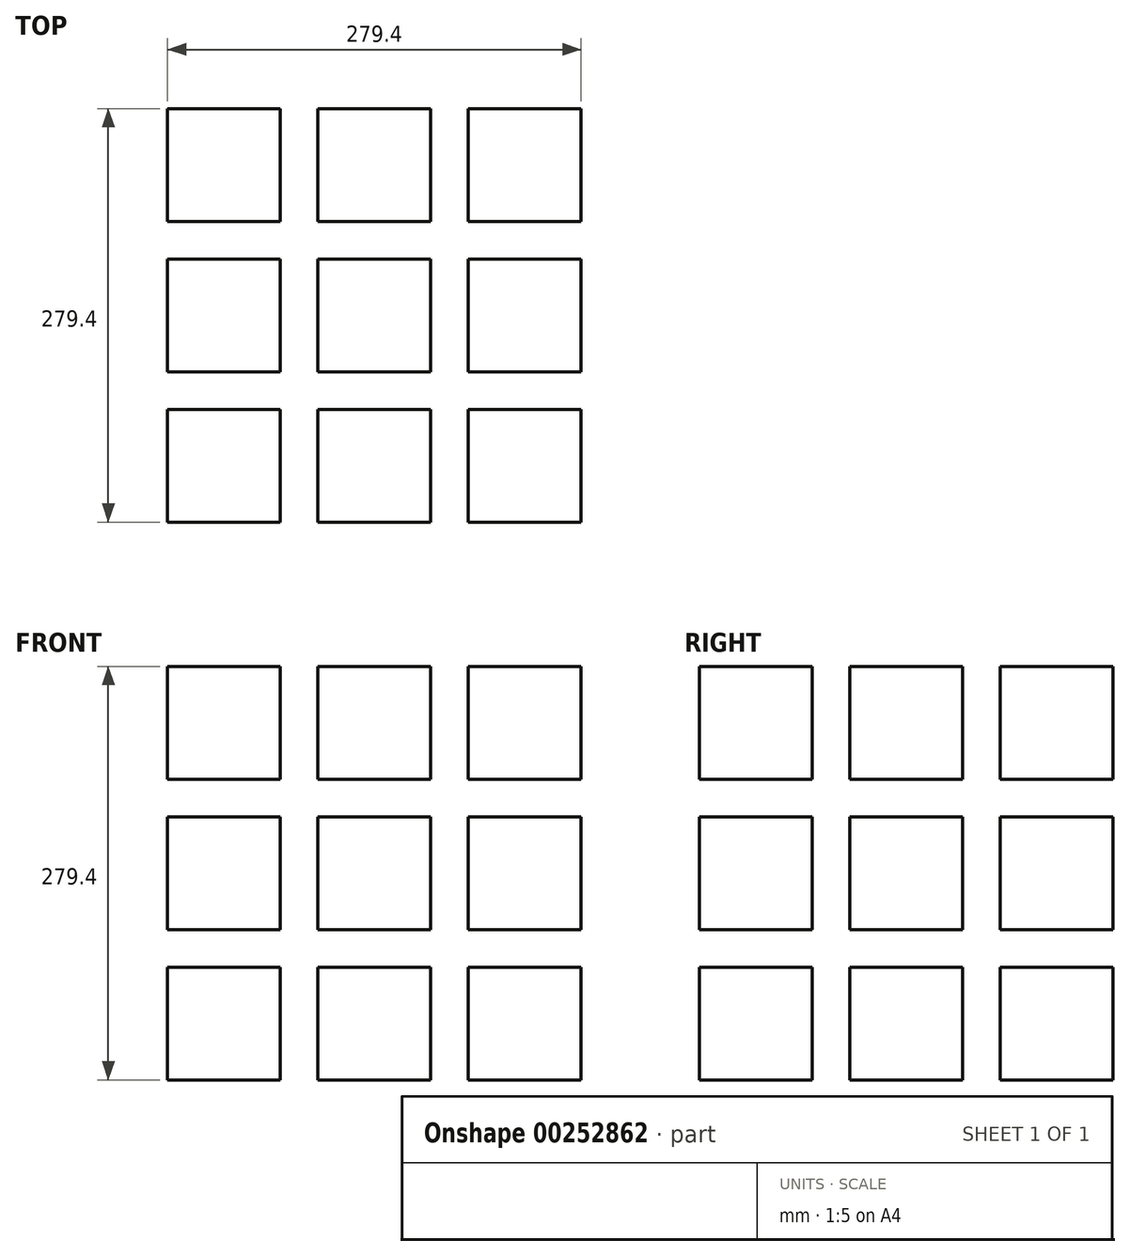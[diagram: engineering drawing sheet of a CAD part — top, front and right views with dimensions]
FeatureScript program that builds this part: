
annotation { "Feature Type Name" : "Feature", "Feature Type Description" : "" }
export const myFeature = defineFeature(function(context is Context, id is Id, definition is map)
    precondition{}
    {
        {
            var Q0;
            Q0=qCreatedBy(makeId("Top.planeOp"),FACE);
            var sketch = newSketch(context, id + "F0", { "sketchPlane" : qUnion([Q0])});
            skLineSegment(sketch, "E0.bottom", {"start": v(139.7, -139.7) * mm, "end": v(-139.7, -139.7) * mm});
            skLineSegment(sketch, "E0.top", {"start": v(139.7, 139.7) * mm, "end": v(-139.7, 139.7) * mm});
            skLineSegment(sketch, "E0.left", {"start": v(139.7, -139.7) * mm, "end": v(139.7, 139.7) * mm});
            skLineSegment(sketch, "E0.right", {"start": v(-139.7, -139.7) * mm, "end": v(-139.7, 139.7) * mm});
            skPoint(sketch, "E0.middle", {"position": v(0, 0) * mm});
            skSolve(sketch);
        }
        {
            var Q0;
            Q0=makeQuery(id+"F0.imprint","IMPRINT",FACE,{"disambiguationData":[TD([[makeQuery(id+"F0.imprint","IMPRINT",EDGE,{"derivedFrom":sQuery(id+"F0.wireOp",EDGE,"E0.bottom")}),-1.0]])]});
            extrude(context, id + "F1", {"entities" : qUnion([Q0]), "depth" : 279.4 * mm});
        }
        {
            var Q0;
            Q0=makeQuery(id+"F1.opExtrude","CAP_FACE",FACE,{"disambiguationData":[OSD([sQuery(id+"F0.wireOp",EDGE,"E0.bottom"),sQuery(id+"F0.wireOp",EDGE,"E0.top"),sQuery(id+"F0.wireOp",EDGE,"E0.left"),sQuery(id+"F0.wireOp",EDGE,"E0.right")])],"isStart":false});
            var sketch = newSketch(context, id + "F2", { "sketchPlane" : qUnion([Q0])});
            skLineSegment(sketch, "E1.bottom", {"start": v(-63.5, 139.7) * mm, "end": v(-38.1, 139.7) * mm});
            skLineSegment(sketch, "E1.top", {"start": v(-63.5, -139.7) * mm, "end": v(-38.1, -139.7) * mm});
            skLineSegment(sketch, "E1.left", {"start": v(-63.5, 139.7) * mm, "end": v(-63.5, -139.7) * mm});
            skLineSegment(sketch, "E1.right", {"start": v(-38.1, 139.7) * mm, "end": v(-38.1, -139.7) * mm});
            skLineSegment(sketch, "E2.bottom", {"start": v(38.1, 139.7) * mm, "end": v(63.5, 139.7) * mm});
            skLineSegment(sketch, "E2.top", {"start": v(38.1, -139.7) * mm, "end": v(63.5, -139.7) * mm});
            skLineSegment(sketch, "E2.left", {"start": v(38.1, 139.7) * mm, "end": v(38.1, -139.7) * mm});
            skLineSegment(sketch, "E2.right", {"start": v(63.5, 139.7) * mm, "end": v(63.5, -139.7) * mm});
            skLineSegment(sketch, "E3.bottom", {"start": v(-139.7, 63.5) * mm, "end": v(139.7, 63.5) * mm});
            skLineSegment(sketch, "E3.top", {"start": v(-139.7, 38.1) * mm, "end": v(139.7, 38.1) * mm});
            skLineSegment(sketch, "E3.left", {"start": v(-139.7, 63.5) * mm, "end": v(-139.7, 38.1) * mm});
            skLineSegment(sketch, "E3.right", {"start": v(139.7, 63.5) * mm, "end": v(139.7, 38.1) * mm});
            skLineSegment(sketch, "E4.bottom", {"start": v(-139.7, -38.1) * mm, "end": v(139.7, -38.1) * mm});
            skLineSegment(sketch, "E4.top", {"start": v(-139.7, -63.5) * mm, "end": v(139.7, -63.5) * mm});
            skLineSegment(sketch, "E4.left", {"start": v(-139.7, -38.1) * mm, "end": v(-139.7, -63.5) * mm});
            skLineSegment(sketch, "E4.right", {"start": v(139.7, -38.1) * mm, "end": v(139.7, -63.5) * mm});
            skSolve(sketch);
        }
        {
            var Q0;
            Q0 = qSketchRegion(id + "F2", true);
            extrude(context, id + "F3", {"entities" : qUnion([Q0]), "operationType" : NewBodyOperationType.REMOVE, "oppositeDirection" : true, "depth" : 279.4 * mm});
        }
        {
            var Q0;
            {var subQ0=sQuery(id+"F0.wireOp",EDGE,"E0.right");var subQ2=sQuery(id+"F0.wireOp",EDGE,"E0.top");Q0=makeQuery(id+"F3.boolean.opBoolean","SPLIT",FACE,{"disambiguationData":[TD([makeQuery(id+"F1.opExtrude","SWEPT_FACE",FACE,{"disambiguationData":[OSD([subQ2])]})])],"derivedFrom":makeQuery(id+"F1.opExtrude","SWEPT_FACE",FACE,{"disambiguationData":[OSD([subQ0])]})});}
            var sketch = newSketch(context, id + "F4", { "sketchPlane" : qUnion([Q0])});
            skLineSegment(sketch, "E5.bottom", {"start": v(-139.7, 203.2) * mm, "end": v(-63.5, 203.2) * mm});
            skLineSegment(sketch, "E5.top", {"start": v(-139.7, 177.8) * mm, "end": v(-63.5, 177.8) * mm});
            skLineSegment(sketch, "E5.left", {"start": v(-139.7, 203.2) * mm, "end": v(-139.7, 177.8) * mm});
            skLineSegment(sketch, "E5.right", {"start": v(-63.5, 203.2) * mm, "end": v(-63.5, 177.8) * mm});
            skLineSegment(sketch, "E6.bottom", {"start": v(-139.7, 101.6) * mm, "end": v(-63.5, 101.6) * mm});
            skLineSegment(sketch, "E6.top", {"start": v(-139.7, 76.2) * mm, "end": v(-63.5, 76.2) * mm});
            skLineSegment(sketch, "E6.left", {"start": v(-139.7, 101.6) * mm, "end": v(-139.7, 76.2) * mm});
            skLineSegment(sketch, "E6.right", {"start": v(-63.5, 101.6) * mm, "end": v(-63.5, 76.2) * mm});
            skSolve(sketch);
        }
        {
            var Q0;
            Q0 = qSketchRegion(id + "F4", true);
            extrude(context, id + "F5", {"entities" : qUnion([Q0]), "operationType" : NewBodyOperationType.REMOVE, "oppositeDirection" : true, "depth" : 533.4 * mm});
        }
        {
            var Q0;
            {var subQ0=sQuery(id+"F2.wireOp",EDGE,"E1.right");Q0=makeQuery(id+"F3.boolean.opBoolean","COPY",FACE,{"derivedFrom":makeQuery(id+"F3.opExtrude","SWEPT_FACE",FACE,{"disambiguationData":[OSD([subQ0]),TDD([makeQuery(id+"F2.imprint","IMPRINT",EDGE,{"disambiguationData":[TD([[makeQuery(id+"F2.imprint","INTERSECT",VERTEX,{"derivedFrom":[subQ0,sQuery(id+"F2.wireOp",EDGE,"E3.bottom")]}),1.0]])],"derivedFrom":subQ0})])]})});}
            var sketch = newSketch(context, id + "F6", { "sketchPlane" : qUnion([Q0])});
            skLineSegment(sketch, "E7.bottom", {"start": v(-139.7, 203.2) * mm, "end": v(-63.5, 203.2) * mm});
            skLineSegment(sketch, "E7.top", {"start": v(-139.7, 177.8) * mm, "end": v(-63.5, 177.8) * mm});
            skLineSegment(sketch, "E7.left", {"start": v(-139.7, 203.2) * mm, "end": v(-139.7, 177.8) * mm});
            skLineSegment(sketch, "E7.right", {"start": v(-63.5, 203.2) * mm, "end": v(-63.5, 177.8) * mm});
            skLineSegment(sketch, "E8.bottom", {"start": v(-139.7, 101.6) * mm, "end": v(-63.5, 101.6) * mm});
            skLineSegment(sketch, "E8.top", {"start": v(-139.7, 76.2) * mm, "end": v(-63.5, 76.2) * mm});
            skLineSegment(sketch, "E8.left", {"start": v(-139.7, 101.6) * mm, "end": v(-139.7, 76.2) * mm});
            skLineSegment(sketch, "E8.right", {"start": v(-63.5, 101.6) * mm, "end": v(-63.5, 76.2) * mm});
            skSolve(sketch);
        }
        {
            var Q0;
            Q0 = qSketchRegion(id + "F6", true);
            extrude(context, id + "F7", {"entities" : qUnion([Q0]), "operationType" : NewBodyOperationType.REMOVE, "oppositeDirection" : true, "depth" : 533.4 * mm});
        }
        {
            var Q0;
            {var subQ0=sQuery(id+"F2.wireOp",EDGE,"E2.right");Q0=makeQuery(id+"F3.boolean.opBoolean","COPY",FACE,{"derivedFrom":makeQuery(id+"F3.opExtrude","SWEPT_FACE",FACE,{"disambiguationData":[OSD([subQ0]),TDD([makeQuery(id+"F2.imprint","IMPRINT",EDGE,{"disambiguationData":[TD([[makeQuery(id+"F2.imprint","INTERSECT",VERTEX,{"derivedFrom":[subQ0,sQuery(id+"F2.wireOp",EDGE,"E3.bottom")]}),1.0]])],"derivedFrom":subQ0})])]})});}
            var sketch = newSketch(context, id + "F8", { "sketchPlane" : qUnion([Q0])});
            skLineSegment(sketch, "E9.bottom", {"start": v(-139.7, 203.2) * mm, "end": v(-63.5, 203.2) * mm});
            skLineSegment(sketch, "E9.top", {"start": v(-139.7, 177.8) * mm, "end": v(-63.5, 177.8) * mm});
            skLineSegment(sketch, "E9.left", {"start": v(-139.7, 203.2) * mm, "end": v(-139.7, 177.8) * mm});
            skLineSegment(sketch, "E9.right", {"start": v(-63.5, 203.2) * mm, "end": v(-63.5, 177.8) * mm});
            skLineSegment(sketch, "E10.bottom", {"start": v(-139.7, 101.6) * mm, "end": v(-63.5, 101.6) * mm});
            skLineSegment(sketch, "E10.top", {"start": v(-139.7, 76.2) * mm, "end": v(-63.5, 76.2) * mm});
            skLineSegment(sketch, "E10.left", {"start": v(-139.7, 101.6) * mm, "end": v(-139.7, 76.2) * mm});
            skLineSegment(sketch, "E10.right", {"start": v(-63.5, 101.6) * mm, "end": v(-63.5, 76.2) * mm});
            skSolve(sketch);
        }
        {
            var Q0;
            Q0 = qSketchRegion(id + "F8", true);
            extrude(context, id + "F9", {"entities" : qUnion([Q0]), "operationType" : NewBodyOperationType.REMOVE, "oppositeDirection" : true, "depth" : 81838.8 * mm});
        }
        {
            var Q0;
            {var subQ0=sQuery(id+"F0.wireOp",EDGE,"E0.right");var subQ6=sQuery(id+"F2.wireOp",EDGE,"E1.left");var subQ7=sQuery(id+"F2.wireOp",EDGE,"E3.top");Q0=makeQuery(id+"F3.boolean.opBoolean","SPLIT",FACE,{"disambiguationData":[TD([makeQuery(id+"F3.opExtrude","SWEPT_FACE",FACE,{"disambiguationData":[OSD([subQ7]),TDD([makeQuery(id+"F2.imprint","IMPRINT",EDGE,{"disambiguationData":[TD([[makeQuery(id+"F2.imprint","INTERSECT",VERTEX,{"derivedFrom":[subQ6,subQ7]}),1.0]])],"derivedFrom":subQ7})])]})])],"derivedFrom":makeQuery(id+"F1.opExtrude","SWEPT_FACE",FACE,{"disambiguationData":[OSD([subQ0])]})});}
            var sketch = newSketch(context, id + "F10", { "sketchPlane" : qUnion([Q0])});
            skLineSegment(sketch, "E11.bottom", {"start": v(-38.1, 203.2) * mm, "end": v(38.1, 203.2) * mm});
            skLineSegment(sketch, "E11.top", {"start": v(-38.1, 177.8) * mm, "end": v(38.1, 177.8) * mm});
            skLineSegment(sketch, "E11.left", {"start": v(-38.1, 203.2) * mm, "end": v(-38.1, 177.8) * mm});
            skLineSegment(sketch, "E11.right", {"start": v(38.1, 203.2) * mm, "end": v(38.1, 177.8) * mm});
            skLineSegment(sketch, "E12.bottom", {"start": v(-38.1, 101.6) * mm, "end": v(38.1, 101.6) * mm});
            skLineSegment(sketch, "E12.top", {"start": v(-38.1, 76.2) * mm, "end": v(38.1, 76.2) * mm});
            skLineSegment(sketch, "E12.left", {"start": v(-38.1, 101.6) * mm, "end": v(-38.1, 76.2) * mm});
            skLineSegment(sketch, "E12.right", {"start": v(38.1, 101.6) * mm, "end": v(38.1, 76.2) * mm});
            skSolve(sketch);
        }
        {
            var Q0;
            Q0 = qSketchRegion(id + "F10", true);
            extrude(context, id + "F11", {"entities" : qUnion([Q0]), "operationType" : NewBodyOperationType.REMOVE, "oppositeDirection" : true, "depth" : 1752.6 * mm});
        }
        {
            var Q0;
            {var subQ0=sQuery(id+"F2.wireOp",EDGE,"E1.right");Q0=makeQuery(id+"F3.boolean.opBoolean","COPY",FACE,{"derivedFrom":makeQuery(id+"F3.opExtrude","SWEPT_FACE",FACE,{"disambiguationData":[OSD([subQ0]),TDD([makeQuery(id+"F2.imprint","IMPRINT",EDGE,{"disambiguationData":[TD([[makeQuery(id+"F2.imprint","INTERSECT",VERTEX,{"derivedFrom":[subQ0,sQuery(id+"F2.wireOp",EDGE,"E3.top")]}),-1.0]])],"derivedFrom":subQ0})])]})});}
            var sketch = newSketch(context, id + "F12", { "sketchPlane" : qUnion([Q0])});
            skLineSegment(sketch, "E13", {"start": v(-38.1, 279.4) * mm, "end": v(-38.1, 203.2) * mm});
            skLineSegment(sketch, "E14.bottom", {"start": v(-38.1, 203.2) * mm, "end": v(38.1, 203.2) * mm});
            skLineSegment(sketch, "E14.top", {"start": v(-38.1, 177.8) * mm, "end": v(38.1, 177.8) * mm});
            skLineSegment(sketch, "E14.left", {"start": v(-38.1, 203.2) * mm, "end": v(-38.1, 177.8) * mm});
            skLineSegment(sketch, "E14.right", {"start": v(38.1, 203.2) * mm, "end": v(38.1, 177.8) * mm});
            skLineSegment(sketch, "E15.bottom", {"start": v(-38.1, 101.6) * mm, "end": v(38.1, 101.6) * mm});
            skLineSegment(sketch, "E15.top", {"start": v(-38.1, 76.2) * mm, "end": v(38.1, 76.2) * mm});
            skLineSegment(sketch, "E15.left", {"start": v(-38.1, 101.6) * mm, "end": v(-38.1, 76.2) * mm});
            skLineSegment(sketch, "E15.right", {"start": v(38.1, 101.6) * mm, "end": v(38.1, 76.2) * mm});
            skSolve(sketch);
        }
        {
            var Q0;
            Q0 = qSketchRegion(id + "F12", true);
            extrude(context, id + "F13", {"entities" : qUnion([Q0]), "operationType" : NewBodyOperationType.REMOVE, "oppositeDirection" : true, "depth" : 50876.2 * mm});
        }
        {
            var Q0;
            {var subQ0=sQuery(id+"F2.wireOp",EDGE,"E2.right");Q0=makeQuery(id+"F3.boolean.opBoolean","COPY",FACE,{"derivedFrom":makeQuery(id+"F3.opExtrude","SWEPT_FACE",FACE,{"disambiguationData":[OSD([subQ0]),TDD([makeQuery(id+"F2.imprint","IMPRINT",EDGE,{"disambiguationData":[TD([[makeQuery(id+"F2.imprint","INTERSECT",VERTEX,{"derivedFrom":[subQ0,sQuery(id+"F2.wireOp",EDGE,"E3.top")]}),-1.0]])],"derivedFrom":subQ0})])]})});}
            var sketch = newSketch(context, id + "F14", { "sketchPlane" : qUnion([Q0])});
            skLineSegment(sketch, "E16.bottom", {"start": v(-38.1, 203.2) * mm, "end": v(38.1, 203.2) * mm});
            skLineSegment(sketch, "E16.top", {"start": v(-38.1, 177.8) * mm, "end": v(38.1, 177.8) * mm});
            skLineSegment(sketch, "E16.left", {"start": v(-38.1, 203.2) * mm, "end": v(-38.1, 177.8) * mm});
            skLineSegment(sketch, "E16.right", {"start": v(38.1, 203.2) * mm, "end": v(38.1, 177.8) * mm});
            skLineSegment(sketch, "E17.bottom", {"start": v(-38.1, 101.6) * mm, "end": v(38.1, 101.6) * mm});
            skLineSegment(sketch, "E17.top", {"start": v(-38.1, 76.2) * mm, "end": v(38.1, 76.2) * mm});
            skLineSegment(sketch, "E17.left", {"start": v(-38.1, 101.6) * mm, "end": v(-38.1, 76.2) * mm});
            skLineSegment(sketch, "E17.right", {"start": v(38.1, 101.6) * mm, "end": v(38.1, 76.2) * mm});
            skSolve(sketch);
        }
        {
            var Q0;
            Q0 = qSketchRegion(id + "F14", true);
            extrude(context, id + "F15", {"entities" : qUnion([Q0]), "operationType" : NewBodyOperationType.REMOVE, "oppositeDirection" : true, "depth" : 10668 * mm});
        }
        {
            var Q0;
            {var subQ0=sQuery(id+"F0.wireOp",EDGE,"E0.bottom");var subQ1=sQuery(id+"F0.wireOp",EDGE,"E0.right");Q0=makeQuery(id+"F3.boolean.opBoolean","SPLIT",FACE,{"disambiguationData":[TD([makeQuery(id+"F1.opExtrude","SWEPT_FACE",FACE,{"disambiguationData":[OSD([subQ0])]})])],"derivedFrom":makeQuery(id+"F1.opExtrude","SWEPT_FACE",FACE,{"disambiguationData":[OSD([subQ1])]})});}
            var sketch = newSketch(context, id + "F16", { "sketchPlane" : qUnion([Q0])});
            skLineSegment(sketch, "E18.bottom", {"start": v(63.5, 203.2) * mm, "end": v(139.7, 203.2) * mm});
            skLineSegment(sketch, "E18.top", {"start": v(63.5, 177.8) * mm, "end": v(139.7, 177.8) * mm});
            skLineSegment(sketch, "E18.left", {"start": v(63.5, 203.2) * mm, "end": v(63.5, 177.8) * mm});
            skLineSegment(sketch, "E18.right", {"start": v(139.7, 203.2) * mm, "end": v(139.7, 177.8) * mm});
            skLineSegment(sketch, "E19.bottom", {"start": v(63.5, 101.6) * mm, "end": v(139.7, 101.6) * mm});
            skLineSegment(sketch, "E19.top", {"start": v(63.5, 76.2) * mm, "end": v(139.7, 76.2) * mm});
            skLineSegment(sketch, "E19.left", {"start": v(63.5, 101.6) * mm, "end": v(63.5, 76.2) * mm});
            skLineSegment(sketch, "E19.right", {"start": v(139.7, 101.6) * mm, "end": v(139.7, 76.2) * mm});
            skSolve(sketch);
        }
        {
            var Q0;
            Q0 = qSketchRegion(id + "F16", true);
            extrude(context, id + "F17", {"entities" : qUnion([Q0]), "operationType" : NewBodyOperationType.REMOVE, "oppositeDirection" : true, "depth" : 33959.8 * mm});
        }
        {
            var Q0;
            {var subQ0=sQuery(id+"F2.wireOp",EDGE,"E1.right");Q0=makeQuery(id+"F3.boolean.opBoolean","COPY",FACE,{"derivedFrom":makeQuery(id+"F3.opExtrude","SWEPT_FACE",FACE,{"disambiguationData":[OSD([subQ0]),TDD([makeQuery(id+"F2.imprint","IMPRINT",EDGE,{"disambiguationData":[TD([[makeQuery(id+"F2.imprint","INTERSECT",VERTEX,{"derivedFrom":[subQ0,sQuery(id+"F2.wireOp",EDGE,"E4.top")]}),-1.0]])],"derivedFrom":subQ0})])]})});}
            var sketch = newSketch(context, id + "F18", { "sketchPlane" : qUnion([Q0])});
            skLineSegment(sketch, "E20.bottom", {"start": v(63.5, 203.2) * mm, "end": v(139.7, 203.2) * mm});
            skLineSegment(sketch, "E20.top", {"start": v(63.5, 177.8) * mm, "end": v(139.7, 177.8) * mm});
            skLineSegment(sketch, "E20.left", {"start": v(63.5, 203.2) * mm, "end": v(63.5, 177.8) * mm});
            skLineSegment(sketch, "E20.right", {"start": v(139.7, 203.2) * mm, "end": v(139.7, 177.8) * mm});
            skLineSegment(sketch, "E21.bottom", {"start": v(63.5, 101.6) * mm, "end": v(139.7, 101.6) * mm});
            skLineSegment(sketch, "E21.top", {"start": v(63.5, 76.2) * mm, "end": v(139.7, 76.2) * mm});
            skLineSegment(sketch, "E21.left", {"start": v(63.5, 101.6) * mm, "end": v(63.5, 76.2) * mm});
            skLineSegment(sketch, "E21.right", {"start": v(139.7, 101.6) * mm, "end": v(139.7, 76.2) * mm});
            skSolve(sketch);
        }
        {
            var Q0;
            Q0 = qSketchRegion(id + "F18", true);
            extrude(context, id + "F19", {"entities" : qUnion([Q0]), "operationType" : NewBodyOperationType.REMOVE, "oppositeDirection" : true, "depth" : 132969 * mm});
        }
        {
            var Q0;
            {var subQ0=sQuery(id+"F2.wireOp",EDGE,"E2.right");Q0=makeQuery(id+"F3.boolean.opBoolean","COPY",FACE,{"derivedFrom":makeQuery(id+"F3.opExtrude","SWEPT_FACE",FACE,{"disambiguationData":[OSD([subQ0]),TDD([makeQuery(id+"F2.imprint","IMPRINT",EDGE,{"disambiguationData":[TD([[makeQuery(id+"F2.imprint","INTERSECT",VERTEX,{"derivedFrom":[subQ0,sQuery(id+"F2.wireOp",EDGE,"E4.top")]}),-1.0]])],"derivedFrom":subQ0})])]})});}
            var sketch = newSketch(context, id + "F20", { "sketchPlane" : qUnion([Q0])});
            skLineSegment(sketch, "E22.bottom", {"start": v(63.5, 203.2) * mm, "end": v(139.7, 203.2) * mm});
            skLineSegment(sketch, "E22.top", {"start": v(63.5, 177.8) * mm, "end": v(139.7, 177.8) * mm});
            skLineSegment(sketch, "E22.left", {"start": v(63.5, 203.2) * mm, "end": v(63.5, 177.8) * mm});
            skLineSegment(sketch, "E22.right", {"start": v(139.7, 203.2) * mm, "end": v(139.7, 177.8) * mm});
            skLineSegment(sketch, "E23.bottom", {"start": v(63.5, 101.6) * mm, "end": v(139.7, 101.6) * mm});
            skLineSegment(sketch, "E23.top", {"start": v(63.5, 76.2) * mm, "end": v(139.7, 76.2) * mm});
            skLineSegment(sketch, "E23.left", {"start": v(63.5, 101.6) * mm, "end": v(63.5, 76.2) * mm});
            skLineSegment(sketch, "E23.right", {"start": v(139.7, 101.6) * mm, "end": v(139.7, 76.2) * mm});
            skSolve(sketch);
        }
        {
            var Q0;
            Q0 = qSketchRegion(id + "F20", true);
            extrude(context, id + "F21", {"entities" : qUnion([Q0]), "operationType" : NewBodyOperationType.REMOVE, "oppositeDirection" : true, "depth" : 50850.8 * mm});
        }
    });
